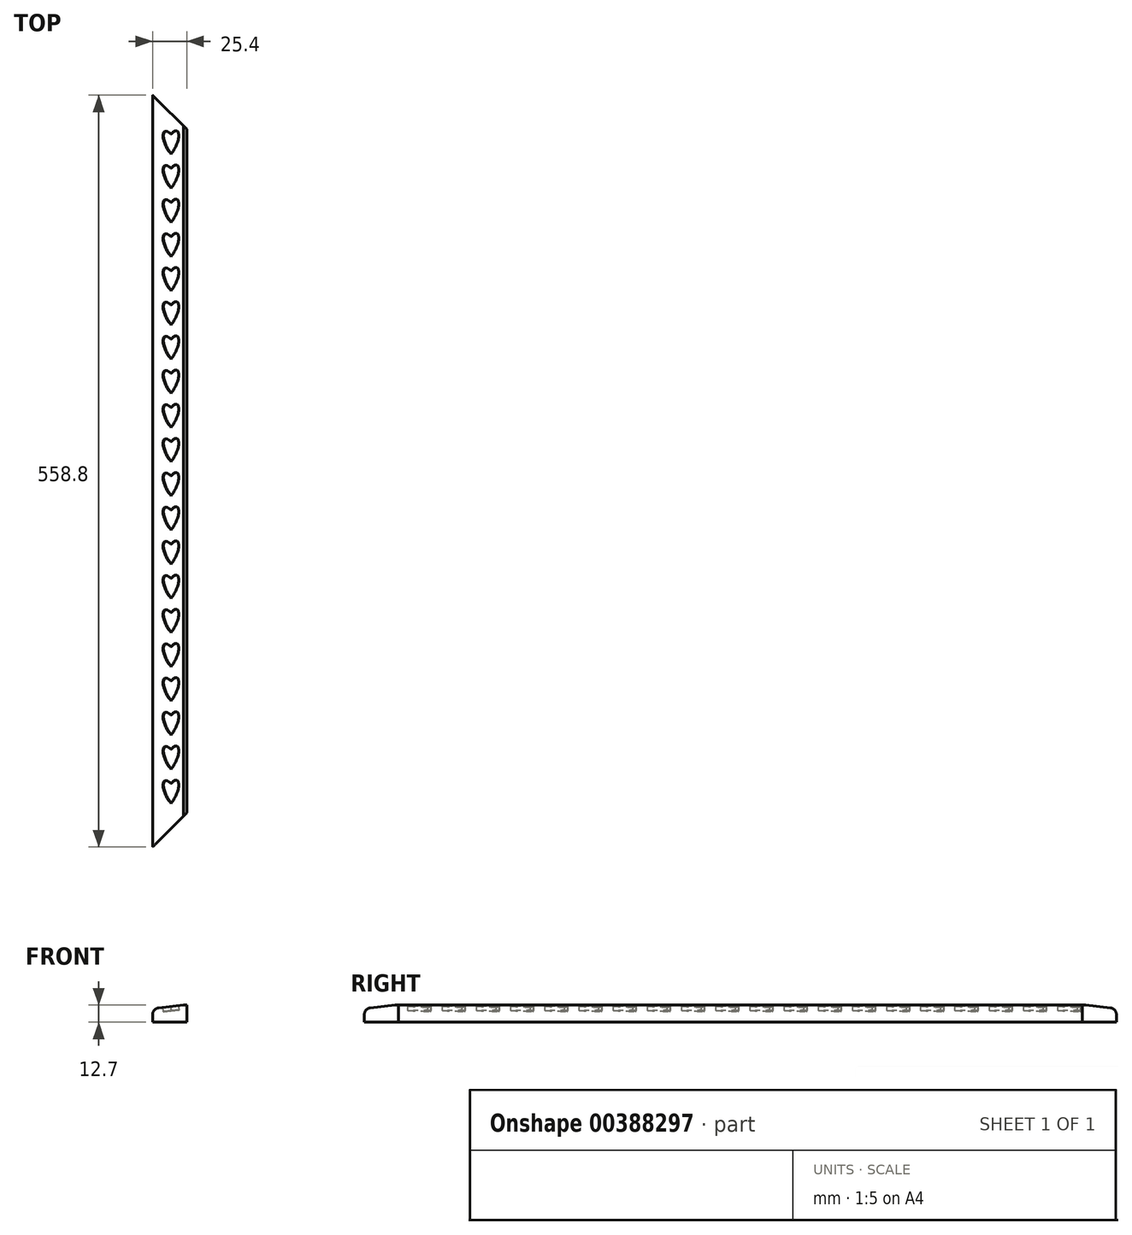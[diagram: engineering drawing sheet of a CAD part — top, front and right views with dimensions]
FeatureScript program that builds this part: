
annotation { "Feature Type Name" : "Feature", "Feature Type Description" : "" }
export const myFeature = defineFeature(function(context is Context, id is Id, definition is map)
    precondition{}
    {
        {
            var Q0;
            Q0=qCreatedBy(makeId("Top.planeOp"),FACE);
            var sketch = newSketch(context, id + "F0", { "sketchPlane" : qUnion([Q0])});
            skLineSegment(sketch, "E0.bottom", {"start": v(-12.7, 279.4) * mm, "end": v(12.7, 279.4) * mm});
            skLineSegment(sketch, "E0.top", {"start": v(-12.7, -279.4) * mm, "end": v(12.7, -279.4) * mm});
            skLineSegment(sketch, "E0.left", {"start": v(-12.7, 279.4) * mm, "end": v(-12.7, -279.4) * mm});
            skLineSegment(sketch, "E0.right", {"start": v(12.7, 279.4) * mm, "end": v(12.7, -279.4) * mm});
            skPoint(sketch, "E0.middle", {"position": v(0, 0) * mm});
            skLineSegment(sketch, "E1", {"start": v(-12.7, -279.4) * mm, "end": v(12.7, -254) * mm});
            skLineSegment(sketch, "E2.MirrorCS", {"start": v(-12.7, 279.4) * mm, "end": v(12.7, 254) * mm});
            skSolve(sketch);
        }
        {
            var Q0;
            Q0=makeQuery(id+"F0.imprint","IMPRINT",FACE,{"disambiguationData":[TD([[makeQuery(id+"F0.imprint","IMPRINT",EDGE,{"derivedFrom":sQuery(id+"F0.wireOp",EDGE,"E0.left")}),1.0]])]});
            extrude(context, id + "F1", {"entities" : qUnion([Q0]), "depth" : 12.7 * mm});
        }
        {
            var Q0;
            Q0=makeQuery(id+"F1.opExtrude","CAP_EDGE",EDGE,{"disambiguationData":[OSD([sQuery(id+"F0.wireOp",EDGE,"E0.left")])],"isStart":false});
            chamfer(context, id + "F2", {"entities" : qUnion([Q0]), "chamferType" : ChamferType.TWO_OFFSETS, "width1" : 2.54 * mm, "oppositeDirection" : true, "width2" : 22.86 * mm, "tangentPropagation" : true});
        }
        {
            var Q0;
            {var subQ0=sQuery(id+"F0.wireOp",EDGE,"E0.left");Q0=makeQuery(id+"F2.opChamfer","BLEND_EDGE",EDGE,{"blendedFrom":[makeQuery(id+"F1.opExtrude","CAP_EDGE",EDGE,{"disambiguationData":[OSD([subQ0])],"isStart":false}),makeQuery(id+"F1.opExtrude","SWEPT_FACE",FACE,{"disambiguationData":[OSD([subQ0])]})],"blendedInto":[makeQuery(id+"F1.opExtrude","SWEPT_FACE",FACE,{"disambiguationData":[OSD([subQ0])]})]});}
            fillet(context, id + "F3", {"entities" : qUnion([Q0]), "radius" : 5.08 * mm, "tangentPropagation" : true, "allowEdgeOverflow" : false});
        }
        {
            var Q0;
            Q0=makeQuery(id+"F2.opChamfer","BLEND_FACE",FACE,{"disambiguationData":[OSD([sQuery(id+"F0.wireOp",EDGE,"E0.left")])]});
            var sketch = newSketch(context, id + "F4", { "sketchPlane" : qUnion([Q0])});
            skLineSegment(sketch, "E3.bottom", {"start": v(-4.41, 253.3) * mm, "end": v(8.96, 253.3) * mm});
            skLineSegment(sketch, "E3.top", {"start": v(-4.41, 232.97) * mm, "end": v(8.96, 232.97) * mm});
            skLineSegment(sketch, "E3.left", {"start": v(-4.41, 253.3) * mm, "end": v(-4.41, 232.97) * mm});
            skLineSegment(sketch, "E3.right", {"start": v(8.96, 253.3) * mm, "end": v(8.96, 232.97) * mm});
            skEllipticalArc(sketch, "E4", {});
            skPoint(sketch, "E4.centerSnap0", {"position": v(-4.41, 243.13) * mm});
            skPoint(sketch, "E4.centerSnap1", {"position": v(2.27, 232.97) * mm});
            skEllipticalArc(sketch, "E5", {});
            skLineSegment(sketch, "E6", {"start": v(2.2, 250.5) * mm, "end": v(2.47, 250.22) * mm});
            skPoint(sketch, "E7.left.start.orphan", {"position": v(-6.95, 255.83) * mm});
            skLineSegment(sketch, "E8.0.1.0", {"start": v(-4.41, 227.9) * mm, "end": v(8.96, 227.9) * mm});
            skPoint(sketch, "E8.0.1.1", {"position": v(2.27, 207.57) * mm});
            skLineSegment(sketch, "E8.0.1.2", {"start": v(-4.41, 227.9) * mm, "end": v(-4.41, 207.57) * mm});
            skLineSegment(sketch, "E8.0.1.4", {"start": v(8.96, 227.9) * mm, "end": v(8.96, 207.57) * mm});
            skPoint(sketch, "E8.0.1.5", {"position": v(-4.41, 217.73) * mm});
            skEllipticalArc(sketch, "E8.0.1.6", {});
            skEllipticalArc(sketch, "E8.0.1.7", {});
            skLineSegment(sketch, "E8.0.1.8", {"start": v(-4.41, 207.57) * mm, "end": v(8.96, 207.57) * mm});
            skLineSegment(sketch, "E8.0.1.9", {"start": v(2.2, 225.1) * mm, "end": v(2.47, 224.82) * mm});
            skLineSegment(sketch, "E8.0.2.0", {"start": v(-4.41, 202.5) * mm, "end": v(8.96, 202.5) * mm});
            skPoint(sketch, "E8.0.2.1", {"position": v(2.27, 182.17) * mm});
            skLineSegment(sketch, "E8.0.2.2", {"start": v(-4.41, 202.5) * mm, "end": v(-4.41, 182.17) * mm});
            skPoint(sketch, "E8.0.2.3", {"position": v(-6.95, 230.43) * mm});
            skLineSegment(sketch, "E8.0.2.4", {"start": v(8.96, 202.5) * mm, "end": v(8.96, 182.17) * mm});
            skPoint(sketch, "E8.0.2.5", {"position": v(-4.41, 192.33) * mm});
            skEllipticalArc(sketch, "E8.0.2.6", {});
            skEllipticalArc(sketch, "E8.0.2.7", {});
            skLineSegment(sketch, "E8.0.2.8", {"start": v(-4.41, 182.17) * mm, "end": v(8.96, 182.17) * mm});
            skLineSegment(sketch, "E8.0.2.9", {"start": v(2.2, 199.7) * mm, "end": v(2.47, 199.42) * mm});
            skLineSegment(sketch, "E8.0.3.0", {"start": v(-4.41, 177.1) * mm, "end": v(8.96, 177.1) * mm});
            skPoint(sketch, "E8.0.3.1", {"position": v(2.27, 156.77) * mm});
            skLineSegment(sketch, "E8.0.3.2", {"start": v(-4.41, 177.1) * mm, "end": v(-4.41, 156.77) * mm});
            skPoint(sketch, "E8.0.3.3", {"position": v(-6.95, 205.03) * mm});
            skLineSegment(sketch, "E8.0.3.4", {"start": v(8.96, 177.1) * mm, "end": v(8.96, 156.77) * mm});
            skPoint(sketch, "E8.0.3.5", {"position": v(-4.41, 166.93) * mm});
            skEllipticalArc(sketch, "E8.0.3.6", {});
            skEllipticalArc(sketch, "E8.0.3.7", {});
            skLineSegment(sketch, "E8.0.3.8", {"start": v(-4.41, 156.77) * mm, "end": v(8.96, 156.77) * mm});
            skLineSegment(sketch, "E8.0.3.9", {"start": v(2.2, 174.3) * mm, "end": v(2.47, 174.02) * mm});
            skLineSegment(sketch, "E8.0.4.0", {"start": v(-4.41, 151.7) * mm, "end": v(8.96, 151.7) * mm});
            skPoint(sketch, "E8.0.4.1", {"position": v(2.27, 131.37) * mm});
            skLineSegment(sketch, "E8.0.4.2", {"start": v(-4.41, 151.7) * mm, "end": v(-4.41, 131.37) * mm});
            skPoint(sketch, "E8.0.4.3", {"position": v(-6.95, 179.63) * mm});
            skLineSegment(sketch, "E8.0.4.4", {"start": v(8.96, 151.7) * mm, "end": v(8.96, 131.37) * mm});
            skPoint(sketch, "E8.0.4.5", {"position": v(-4.41, 141.53) * mm});
            skEllipticalArc(sketch, "E8.0.4.6", {});
            skEllipticalArc(sketch, "E8.0.4.7", {});
            skLineSegment(sketch, "E8.0.4.8", {"start": v(-4.41, 131.37) * mm, "end": v(8.96, 131.37) * mm});
            skLineSegment(sketch, "E8.0.4.9", {"start": v(2.2, 148.9) * mm, "end": v(2.47, 148.62) * mm});
            skLineSegment(sketch, "E8.0.5.0", {"start": v(-4.41, 126.3) * mm, "end": v(8.96, 126.3) * mm});
            skPoint(sketch, "E8.0.5.1", {"position": v(2.27, 105.97) * mm});
            skLineSegment(sketch, "E8.0.5.2", {"start": v(-4.41, 126.3) * mm, "end": v(-4.41, 105.97) * mm});
            skPoint(sketch, "E8.0.5.3", {"position": v(-6.95, 154.23) * mm});
            skLineSegment(sketch, "E8.0.5.4", {"start": v(8.96, 126.3) * mm, "end": v(8.96, 105.97) * mm});
            skPoint(sketch, "E8.0.5.5", {"position": v(-4.41, 116.13) * mm});
            skEllipticalArc(sketch, "E8.0.5.6", {});
            skEllipticalArc(sketch, "E8.0.5.7", {});
            skLineSegment(sketch, "E8.0.5.8", {"start": v(-4.41, 105.97) * mm, "end": v(8.96, 105.97) * mm});
            skLineSegment(sketch, "E8.0.5.9", {"start": v(2.2, 123.5) * mm, "end": v(2.47, 123.22) * mm});
            skLineSegment(sketch, "E8.0.6.0", {"start": v(-4.41, 100.9) * mm, "end": v(8.96, 100.9) * mm});
            skPoint(sketch, "E8.0.6.1", {"position": v(2.27, 80.57) * mm});
            skLineSegment(sketch, "E8.0.6.2", {"start": v(-4.41, 100.9) * mm, "end": v(-4.41, 80.57) * mm});
            skPoint(sketch, "E8.0.6.3", {"position": v(-6.95, 128.83) * mm});
            skLineSegment(sketch, "E8.0.6.4", {"start": v(8.96, 100.9) * mm, "end": v(8.96, 80.57) * mm});
            skPoint(sketch, "E8.0.6.5", {"position": v(-4.41, 90.73) * mm});
            skEllipticalArc(sketch, "E8.0.6.6", {});
            skEllipticalArc(sketch, "E8.0.6.7", {});
            skLineSegment(sketch, "E8.0.6.8", {"start": v(-4.41, 80.57) * mm, "end": v(8.96, 80.57) * mm});
            skLineSegment(sketch, "E8.0.6.9", {"start": v(2.2, 98.1) * mm, "end": v(2.47, 97.82) * mm});
            skLineSegment(sketch, "E8.0.7.0", {"start": v(-4.41, 75.5) * mm, "end": v(8.96, 75.5) * mm});
            skPoint(sketch, "E8.0.7.1", {"position": v(2.27, 55.17) * mm});
            skLineSegment(sketch, "E8.0.7.2", {"start": v(-4.41, 75.5) * mm, "end": v(-4.41, 55.17) * mm});
            skPoint(sketch, "E8.0.7.3", {"position": v(-6.95, 103.43) * mm});
            skLineSegment(sketch, "E8.0.7.4", {"start": v(8.96, 75.5) * mm, "end": v(8.96, 55.17) * mm});
            skPoint(sketch, "E8.0.7.5", {"position": v(-4.41, 65.33) * mm});
            skEllipticalArc(sketch, "E8.0.7.6", {});
            skEllipticalArc(sketch, "E8.0.7.7", {});
            skLineSegment(sketch, "E8.0.7.8", {"start": v(-4.41, 55.17) * mm, "end": v(8.96, 55.17) * mm});
            skLineSegment(sketch, "E8.0.7.9", {"start": v(2.2, 72.7) * mm, "end": v(2.47, 72.42) * mm});
            skLineSegment(sketch, "E8.0.8.0", {"start": v(-4.41, 50.1) * mm, "end": v(8.96, 50.1) * mm});
            skPoint(sketch, "E8.0.8.1", {"position": v(2.27, 29.77) * mm});
            skLineSegment(sketch, "E8.0.8.2", {"start": v(-4.41, 50.1) * mm, "end": v(-4.41, 29.77) * mm});
            skPoint(sketch, "E8.0.8.3", {"position": v(-6.95, 78.03) * mm});
            skLineSegment(sketch, "E8.0.8.4", {"start": v(8.96, 50.1) * mm, "end": v(8.96, 29.77) * mm});
            skPoint(sketch, "E8.0.8.5", {"position": v(-4.41, 39.93) * mm});
            skEllipticalArc(sketch, "E8.0.8.6", {});
            skEllipticalArc(sketch, "E8.0.8.7", {});
            skLineSegment(sketch, "E8.0.8.8", {"start": v(-4.41, 29.77) * mm, "end": v(8.96, 29.77) * mm});
            skLineSegment(sketch, "E8.0.8.9", {"start": v(2.2, 47.3) * mm, "end": v(2.47, 47.02) * mm});
            skLineSegment(sketch, "E8.0.9.0", {"start": v(-4.41, 24.7) * mm, "end": v(8.96, 24.7) * mm});
            skPoint(sketch, "E8.0.9.1", {"position": v(2.27, 4.37) * mm});
            skLineSegment(sketch, "E8.0.9.2", {"start": v(-4.41, 24.7) * mm, "end": v(-4.41, 4.37) * mm});
            skPoint(sketch, "E8.0.9.3", {"position": v(-6.95, 52.63) * mm});
            skLineSegment(sketch, "E8.0.9.4", {"start": v(8.96, 24.7) * mm, "end": v(8.96, 4.37) * mm});
            skPoint(sketch, "E8.0.9.5", {"position": v(-4.41, 14.53) * mm});
            skEllipticalArc(sketch, "E8.0.9.6", {});
            skEllipticalArc(sketch, "E8.0.9.7", {});
            skLineSegment(sketch, "E8.0.9.8", {"start": v(-4.41, 4.37) * mm, "end": v(8.96, 4.37) * mm});
            skLineSegment(sketch, "E8.0.9.9", {"start": v(2.2, 21.9) * mm, "end": v(2.47, 21.62) * mm});
            skLineSegment(sketch, "E8.0.10.0", {"start": v(-4.41, -0.7) * mm, "end": v(8.96, -0.7) * mm});
            skPoint(sketch, "E8.0.10.1", {"position": v(2.27, -21.03) * mm});
            skLineSegment(sketch, "E8.0.10.2", {"start": v(-4.41, -0.7) * mm, "end": v(-4.41, -21.03) * mm});
            skPoint(sketch, "E8.0.10.3", {"position": v(-6.95, 27.23) * mm});
            skLineSegment(sketch, "E8.0.10.4", {"start": v(8.96, -0.7) * mm, "end": v(8.96, -21.03) * mm});
            skPoint(sketch, "E8.0.10.5", {"position": v(-4.41, -10.87) * mm});
            skEllipticalArc(sketch, "E8.0.10.6", {});
            skEllipticalArc(sketch, "E8.0.10.7", {});
            skLineSegment(sketch, "E8.0.10.8", {"start": v(-4.41, -21.03) * mm, "end": v(8.96, -21.03) * mm});
            skLineSegment(sketch, "E8.0.10.9", {"start": v(2.2, -3.5) * mm, "end": v(2.47, -3.78) * mm});
            skLineSegment(sketch, "E8.0.11.0", {"start": v(-4.41, -26.1) * mm, "end": v(8.96, -26.1) * mm});
            skPoint(sketch, "E8.0.11.1", {"position": v(2.27, -46.43) * mm});
            skLineSegment(sketch, "E8.0.11.2", {"start": v(-4.41, -26.1) * mm, "end": v(-4.41, -46.43) * mm});
            skPoint(sketch, "E8.0.11.3", {"position": v(-6.95, 1.83) * mm});
            skLineSegment(sketch, "E8.0.11.4", {"start": v(8.96, -26.1) * mm, "end": v(8.96, -46.43) * mm});
            skPoint(sketch, "E8.0.11.5", {"position": v(-4.41, -36.27) * mm});
            skEllipticalArc(sketch, "E8.0.11.6", {});
            skEllipticalArc(sketch, "E8.0.11.7", {});
            skLineSegment(sketch, "E8.0.11.8", {"start": v(-4.41, -46.43) * mm, "end": v(8.96, -46.43) * mm});
            skLineSegment(sketch, "E8.0.11.9", {"start": v(2.2, -28.9) * mm, "end": v(2.47, -29.18) * mm});
            skLineSegment(sketch, "E8.0.12.0", {"start": v(-4.41, -51.5) * mm, "end": v(8.96, -51.5) * mm});
            skPoint(sketch, "E8.0.12.1", {"position": v(2.27, -71.83) * mm});
            skLineSegment(sketch, "E8.0.12.2", {"start": v(-4.41, -51.5) * mm, "end": v(-4.41, -71.83) * mm});
            skPoint(sketch, "E8.0.12.3", {"position": v(-6.95, -23.57) * mm});
            skLineSegment(sketch, "E8.0.12.4", {"start": v(8.96, -51.5) * mm, "end": v(8.96, -71.83) * mm});
            skPoint(sketch, "E8.0.12.5", {"position": v(-4.41, -61.67) * mm});
            skEllipticalArc(sketch, "E8.0.12.6", {});
            skEllipticalArc(sketch, "E8.0.12.7", {});
            skLineSegment(sketch, "E8.0.12.8", {"start": v(-4.41, -71.83) * mm, "end": v(8.96, -71.83) * mm});
            skLineSegment(sketch, "E8.0.12.9", {"start": v(2.2, -54.3) * mm, "end": v(2.47, -54.58) * mm});
            skLineSegment(sketch, "E8.0.13.0", {"start": v(-4.41, -76.9) * mm, "end": v(8.96, -76.9) * mm});
            skPoint(sketch, "E8.0.13.1", {"position": v(2.27, -97.23) * mm});
            skLineSegment(sketch, "E8.0.13.2", {"start": v(-4.41, -76.9) * mm, "end": v(-4.41, -97.23) * mm});
            skPoint(sketch, "E8.0.13.3", {"position": v(-6.95, -48.97) * mm});
            skLineSegment(sketch, "E8.0.13.4", {"start": v(8.96, -76.9) * mm, "end": v(8.96, -97.23) * mm});
            skPoint(sketch, "E8.0.13.5", {"position": v(-4.41, -87.07) * mm});
            skEllipticalArc(sketch, "E8.0.13.6", {});
            skEllipticalArc(sketch, "E8.0.13.7", {});
            skLineSegment(sketch, "E8.0.13.8", {"start": v(-4.41, -97.23) * mm, "end": v(8.96, -97.23) * mm});
            skLineSegment(sketch, "E8.0.13.9", {"start": v(2.2, -79.7) * mm, "end": v(2.47, -79.98) * mm});
            skLineSegment(sketch, "E8.0.14.0", {"start": v(-4.41, -102.3) * mm, "end": v(8.96, -102.3) * mm});
            skPoint(sketch, "E8.0.14.1", {"position": v(2.27, -122.63) * mm});
            skLineSegment(sketch, "E8.0.14.2", {"start": v(-4.41, -102.3) * mm, "end": v(-4.41, -122.63) * mm});
            skPoint(sketch, "E8.0.14.3", {"position": v(-6.95, -74.37) * mm});
            skLineSegment(sketch, "E8.0.14.4", {"start": v(8.96, -102.3) * mm, "end": v(8.96, -122.63) * mm});
            skPoint(sketch, "E8.0.14.5", {"position": v(-4.41, -112.47) * mm});
            skEllipticalArc(sketch, "E8.0.14.6", {});
            skEllipticalArc(sketch, "E8.0.14.7", {});
            skLineSegment(sketch, "E8.0.14.8", {"start": v(-4.41, -122.63) * mm, "end": v(8.96, -122.63) * mm});
            skLineSegment(sketch, "E8.0.14.9", {"start": v(2.2, -105.1) * mm, "end": v(2.47, -105.38) * mm});
            skLineSegment(sketch, "E8.0.15.0", {"start": v(-4.41, -127.7) * mm, "end": v(8.96, -127.7) * mm});
            skPoint(sketch, "E8.0.15.1", {"position": v(2.27, -148.03) * mm});
            skLineSegment(sketch, "E8.0.15.2", {"start": v(-4.41, -127.7) * mm, "end": v(-4.41, -148.03) * mm});
            skPoint(sketch, "E8.0.15.3", {"position": v(-6.95, -99.77) * mm});
            skLineSegment(sketch, "E8.0.15.4", {"start": v(8.96, -127.7) * mm, "end": v(8.96, -148.03) * mm});
            skPoint(sketch, "E8.0.15.5", {"position": v(-4.41, -137.87) * mm});
            skEllipticalArc(sketch, "E8.0.15.6", {});
            skEllipticalArc(sketch, "E8.0.15.7", {});
            skLineSegment(sketch, "E8.0.15.8", {"start": v(-4.41, -148.03) * mm, "end": v(8.96, -148.03) * mm});
            skLineSegment(sketch, "E8.0.15.9", {"start": v(2.2, -130.5) * mm, "end": v(2.47, -130.78) * mm});
            skLineSegment(sketch, "E8.0.16.0", {"start": v(-4.41, -153.1) * mm, "end": v(8.96, -153.1) * mm});
            skPoint(sketch, "E8.0.16.1", {"position": v(2.27, -173.43) * mm});
            skLineSegment(sketch, "E8.0.16.2", {"start": v(-4.41, -153.1) * mm, "end": v(-4.41, -173.43) * mm});
            skPoint(sketch, "E8.0.16.3", {"position": v(-6.95, -125.17) * mm});
            skLineSegment(sketch, "E8.0.16.4", {"start": v(8.96, -153.1) * mm, "end": v(8.96, -173.43) * mm});
            skPoint(sketch, "E8.0.16.5", {"position": v(-4.41, -163.27) * mm});
            skEllipticalArc(sketch, "E8.0.16.6", {});
            skEllipticalArc(sketch, "E8.0.16.7", {});
            skLineSegment(sketch, "E8.0.16.8", {"start": v(-4.41, -173.43) * mm, "end": v(8.96, -173.43) * mm});
            skLineSegment(sketch, "E8.0.16.9", {"start": v(2.2, -155.9) * mm, "end": v(2.47, -156.18) * mm});
            skLineSegment(sketch, "E8.0.17.0", {"start": v(-4.41, -178.5) * mm, "end": v(8.96, -178.5) * mm});
            skPoint(sketch, "E8.0.17.1", {"position": v(2.27, -198.83) * mm});
            skLineSegment(sketch, "E8.0.17.2", {"start": v(-4.41, -178.5) * mm, "end": v(-4.41, -198.83) * mm});
            skPoint(sketch, "E8.0.17.3", {"position": v(-6.95, -150.57) * mm});
            skLineSegment(sketch, "E8.0.17.4", {"start": v(8.96, -178.5) * mm, "end": v(8.96, -198.83) * mm});
            skPoint(sketch, "E8.0.17.5", {"position": v(-4.41, -188.67) * mm});
            skEllipticalArc(sketch, "E8.0.17.6", {});
            skEllipticalArc(sketch, "E8.0.17.7", {});
            skLineSegment(sketch, "E8.0.17.8", {"start": v(-4.41, -198.83) * mm, "end": v(8.96, -198.83) * mm});
            skLineSegment(sketch, "E8.0.17.9", {"start": v(2.2, -181.3) * mm, "end": v(2.47, -181.58) * mm});
            skLineSegment(sketch, "E8.direction1", {"start": v(-4.41, 232.97) * mm, "end": v(20.99, 232.97) * mm, "construction": true});
            skLineSegment(sketch, "E8.direction2", {"start": v(-4.41, 232.97) * mm, "end": v(-4.41, 207.57) * mm, "construction": true});
            skPoint(sketch, "E9.0.1.0", {"position": v(2.27, -224.23) * mm});
            skPoint(sketch, "E9.0.1.2", {"position": v(-4.41, -214.07) * mm});
            skLineSegment(sketch, "E9.0.1.3", {"start": v(-4.41, -203.9) * mm, "end": v(8.96, -203.9) * mm});
            skLineSegment(sketch, "E9.0.1.4", {"start": v(-4.41, -203.9) * mm, "end": v(-4.41, -224.23) * mm});
            skLineSegment(sketch, "E9.0.1.5", {"start": v(8.96, -203.9) * mm, "end": v(8.96, -224.23) * mm});
            skEllipticalArc(sketch, "E9.0.1.6", {});
            skEllipticalArc(sketch, "E9.0.1.7", {});
            skLineSegment(sketch, "E9.0.1.8", {"start": v(-4.41, -224.23) * mm, "end": v(8.96, -224.23) * mm});
            skLineSegment(sketch, "E9.0.1.9", {"start": v(2.2, -206.7) * mm, "end": v(2.47, -206.98) * mm});
            skPoint(sketch, "E9.0.2.0", {"position": v(2.27, -249.63) * mm});
            skPoint(sketch, "E9.0.2.1", {"position": v(2.27, -224.23) * mm});
            skPoint(sketch, "E9.0.2.2", {"position": v(-4.41, -239.47) * mm});
            skLineSegment(sketch, "E9.0.2.3", {"start": v(-4.41, -229.3) * mm, "end": v(8.96, -229.3) * mm});
            skLineSegment(sketch, "E9.0.2.4", {"start": v(-4.41, -229.3) * mm, "end": v(-4.41, -249.63) * mm});
            skLineSegment(sketch, "E9.0.2.5", {"start": v(8.96, -229.3) * mm, "end": v(8.96, -249.63) * mm});
            skEllipticalArc(sketch, "E9.0.2.6", {});
            skEllipticalArc(sketch, "E9.0.2.7", {});
            skLineSegment(sketch, "E9.0.2.8", {"start": v(-4.41, -249.63) * mm, "end": v(8.96, -249.63) * mm});
            skLineSegment(sketch, "E9.0.2.9", {"start": v(2.2, -232.1) * mm, "end": v(2.47, -232.38) * mm});
            skLineSegment(sketch, "E9.direction1", {"start": v(-4.41, -198.83) * mm, "end": v(20.99, -198.83) * mm, "construction": true});
            skLineSegment(sketch, "E9.direction2", {"start": v(-4.41, -198.83) * mm, "end": v(-4.41, -224.23) * mm, "construction": true});
            const initialGuessF4  = {"E4": [0.002273408694541042, 0.24313099215246017, -0.44549528212436185, 0.8952842864727022, 0.0104013, 0.0041656, 5.4030752140367095, 2.2614825604469164], "E5": [0.002273408694541042, 0.24313099215246017, 0.42639124113221455, 0.9045388380195346, 0.0106934, 0.004089400000000001, 4.043989840250925, 0.902397186661131], "E8.0.1.6": [0.002273408694541042, 0.21773099215246017, 0.42639124113221455, 0.9045388380195346, 0.0106934, 0.004089400000000001, 4.043989840250925, 0.9023971866611309], "E8.0.1.7": [0.002273408694541042, 0.21773099215246017, -0.44549528212436185, 0.8952842864727022, 0.0104013, 0.0041656, 5.4030752140367095, 2.2614825604469164], "E8.0.2.6": [0.002273408694541042, 0.19233099215246016, 0.42639124113221455, 0.9045388380195346, 0.0106934, 0.004089400000000001, 4.043989840250925, 0.9023971866611309], "E8.0.2.7": [0.002273408694541042, 0.19233099215246016, -0.44549528212436185, 0.8952842864727022, 0.0104013, 0.0041656, 5.4030752140367095, 2.2614825604469164], "E8.0.3.6": [0.002273408694541042, 0.16693099215246016, 0.42639124113221455, 0.9045388380195346, 0.0106934, 0.004089400000000001, 4.043989840250925, 0.9023971866611309], "E8.0.3.7": [0.002273408694541042, 0.16693099215246016, -0.44549528212436185, 0.8952842864727022, 0.0104013, 0.0041656, 5.4030752140367095, 2.2614825604469164], "E8.0.4.6": [0.002273408694541042, 0.14153099215246015, 0.42639124113221455, 0.9045388380195346, 0.0106934, 0.004089400000000001, 4.043989840250925, 0.9023971866611309], "E8.0.4.7": [0.002273408694541042, 0.14153099215246015, -0.44549528212436185, 0.8952842864727022, 0.0104013, 0.0041656, 5.4030752140367095, 2.2614825604469164], "E8.0.5.6": [0.002273408694541042, 0.11613099215246014, 0.42639124113221455, 0.9045388380195346, 0.0106934, 0.004089400000000001, 4.043989840250925, 0.9023971866611309], "E8.0.5.7": [0.002273408694541042, 0.11613099215246014, -0.44549528212436185, 0.8952842864727022, 0.0104013, 0.0041656, 5.4030752140367095, 2.2614825604469164], "E8.0.6.6": [0.002273408694541042, 0.09073099215246014, 0.42639124113221455, 0.9045388380195346, 0.0106934, 0.004089400000000001, 4.043989840250925, 0.9023971866611309], "E8.0.6.7": [0.002273408694541042, 0.09073099215246014, -0.44549528212436185, 0.8952842864727022, 0.0104013, 0.0041656, 5.4030752140367095, 2.2614825604469164], "E8.0.7.6": [0.002273408694541042, 0.06533099215246013, 0.42639124113221455, 0.9045388380195346, 0.0106934, 0.004089400000000001, 4.043989840250925, 0.9023971866611309], "E8.0.7.7": [0.002273408694541042, 0.06533099215246013, -0.44549528212436185, 0.8952842864727022, 0.0104013, 0.0041656, 5.4030752140367095, 2.2614825604469164], "E8.0.8.6": [0.002273408694541042, 0.039930992152460126, 0.42639124113221455, 0.9045388380195346, 0.0106934, 0.004089400000000001, 4.043989840250925, 0.9023971866611309], "E8.0.8.7": [0.002273408694541042, 0.039930992152460126, -0.44549528212436185, 0.8952842864727022, 0.0104013, 0.0041656, 5.4030752140367095, 2.261482560446917], "E8.0.9.6": [0.002273408694541042, 0.014530992152460117, 0.42639124113221455, 0.9045388380195346, 0.0106934, 0.004089400000000001, 4.043989840250925, 0.9023971866611309], "E8.0.9.7": [0.002273408694541042, 0.014530992152460117, -0.44549528212436185, 0.8952842864727022, 0.0104013, 0.0041656, 5.4030752140367095, 2.2614825604469164], "E8.0.10.6": [0.002273408694541042, -0.010869007847539889, 0.42639124113221455, 0.9045388380195346, 0.0106934, 0.004089400000000001, 4.043989840250925, 0.9023971866611309], "E8.0.10.7": [0.002273408694541042, -0.010869007847539889, -0.44549528212436185, 0.8952842864727022, 0.0104013, 0.0041656, 5.4030752140367095, 2.2614825604469164], "E8.0.11.6": [0.002273408694541042, -0.03626900784753992, 0.42639124113221455, 0.9045388380195346, 0.0106934, 0.004089400000000001, 4.043989840250925, 0.9023971866611309], "E8.0.11.7": [0.002273408694541042, -0.03626900784753992, -0.44549528212436185, 0.8952842864727022, 0.0104013, 0.0041656, 5.4030752140367095, 2.2614825604469164], "E8.0.12.6": [0.002273408694541042, -0.0616690078475399, 0.42639124113221455, 0.9045388380195346, 0.0106934, 0.004089400000000001, 4.043989840250925, 0.9023971866611309], "E8.0.12.7": [0.002273408694541042, -0.0616690078475399, -0.44549528212436185, 0.8952842864727022, 0.0104013, 0.0041656, 5.4030752140367095, 2.2614825604469164], "E8.0.13.6": [0.002273408694541042, -0.08706900784753988, 0.42639124113221455, 0.9045388380195346, 0.0106934, 0.004089400000000001, 4.043989840250925, 0.9023971866611309], "E8.0.13.7": [0.002273408694541042, -0.08706900784753988, -0.44549528212436185, 0.8952842864727022, 0.0104013, 0.0041656, 5.4030752140367095, 2.2614825604469164], "E8.0.14.6": [0.002273408694541042, -0.11246900784753991, 0.42639124113221455, 0.9045388380195346, 0.0106934, 0.004089400000000001, 4.043989840250925, 0.9023971866611309], "E8.0.14.7": [0.002273408694541042, -0.11246900784753991, -0.44549528212436185, 0.8952842864727022, 0.0104013, 0.0041656, 5.4030752140367095, 2.2614825604469164], "E8.0.15.6": [0.002273408694541042, -0.13786900784753994, 0.42639124113221455, 0.9045388380195346, 0.0106934, 0.004089400000000001, 4.043989840250925, 0.9023971866611309], "E8.0.15.7": [0.002273408694541042, -0.13786900784753994, -0.44549528212436185, 0.8952842864727022, 0.0104013, 0.0041656, 5.4030752140367095, 2.2614825604469164], "E8.0.16.6": [0.002273408694541042, -0.16326900784753992, 0.42639124113221455, 0.9045388380195346, 0.0106934, 0.004089400000000001, 4.043989840250925, 0.9023971866611309], "E8.0.16.7": [0.002273408694541042, -0.16326900784753992, -0.44549528212436185, 0.8952842864727022, 0.0104013, 0.0041656, 5.4030752140367095, 2.2614825604469164], "E8.0.17.6": [0.002273408694541042, -0.1886690078475399, 0.42639124113221455, 0.9045388380195346, 0.0106934, 0.004089400000000001, 4.043989840250925, 0.9023971866611309], "E8.0.17.7": [0.002273408694541042, -0.1886690078475399, -0.44549528212436185, 0.8952842864727022, 0.0104013, 0.0041656, 5.4030752140367095, 2.2614825604469164], "E9.0.1.6": [0.002273408694541042, -0.2140690078475399, 0.42639124113221455, 0.9045388380195346, 0.0106934, 0.004089400000000001, 4.043989840250925, 0.9023971866611308], "E9.0.1.7": [0.002273408694541042, -0.2140690078475399, -0.44549528212436185, 0.8952842864727022, 0.0104013, 0.0041656, 5.4030752140367095, 2.2614825604469164], "E9.0.2.6": [0.002273408694541042, -0.2394690078475399, 0.42639124113221455, 0.9045388380195346, 0.0106934, 0.004089400000000001, 4.043989840250925, 0.9023971866611308], "E9.0.2.7": [0.002273408694541042, -0.2394690078475399, -0.44549528212436185, 0.8952842864727022, 0.0104013, 0.0041656, 5.4030752140367095, 2.2614825604469164]};
            skSetInitialGuess(sketch, initialGuessF4);
            skSolve(sketch);
        }
        {
            var Q0;
            Q0=makeQuery(id+"F4.imprint","IMPRINT",FACE,{"disambiguationData":[TD([[makeQuery(id+"F4.imprint","IMPRINT",EDGE,{"derivedFrom":sQuery(id+"F4.wireOp",EDGE,"E4")}),1.0]])]});
            var Q1;
            Q1=makeQuery(id+"F4.imprint","IMPRINT",FACE,{"disambiguationData":[TD([[makeQuery(id+"F4.imprint","IMPRINT",EDGE,{"derivedFrom":sQuery(id+"F4.wireOp",EDGE,"E8.0.1.6")}),1.0]])]});
            var Q2;
            Q2=makeQuery(id+"F4.imprint","IMPRINT",FACE,{"disambiguationData":[TD([[makeQuery(id+"F4.imprint","IMPRINT",EDGE,{"derivedFrom":sQuery(id+"F4.wireOp",EDGE,"E8.0.2.6")}),1.0]])]});
            var Q3;
            Q3=makeQuery(id+"F4.imprint","IMPRINT",FACE,{"disambiguationData":[TD([[makeQuery(id+"F4.imprint","IMPRINT",EDGE,{"derivedFrom":sQuery(id+"F4.wireOp",EDGE,"E8.0.3.6")}),1.0]])]});
            var Q4;
            Q4=makeQuery(id+"F4.imprint","IMPRINT",FACE,{"disambiguationData":[TD([[makeQuery(id+"F4.imprint","IMPRINT",EDGE,{"derivedFrom":sQuery(id+"F4.wireOp",EDGE,"E8.0.4.6")}),1.0]])]});
            var Q5;
            Q5=makeQuery(id+"F4.imprint","IMPRINT",FACE,{"disambiguationData":[TD([[makeQuery(id+"F4.imprint","IMPRINT",EDGE,{"derivedFrom":sQuery(id+"F4.wireOp",EDGE,"E8.0.5.6")}),1.0]])]});
            var Q6;
            Q6=makeQuery(id+"F4.imprint","IMPRINT",FACE,{"disambiguationData":[TD([[makeQuery(id+"F4.imprint","IMPRINT",EDGE,{"derivedFrom":sQuery(id+"F4.wireOp",EDGE,"E8.0.6.6")}),1.0]])]});
            var Q7;
            Q7=makeQuery(id+"F4.imprint","IMPRINT",FACE,{"disambiguationData":[TD([[makeQuery(id+"F4.imprint","IMPRINT",EDGE,{"derivedFrom":sQuery(id+"F4.wireOp",EDGE,"E8.0.7.6")}),1.0]])]});
            var Q8;
            Q8=makeQuery(id+"F4.imprint","IMPRINT",FACE,{"disambiguationData":[TD([[makeQuery(id+"F4.imprint","IMPRINT",EDGE,{"derivedFrom":sQuery(id+"F4.wireOp",EDGE,"E8.0.8.6")}),1.0]])]});
            var Q9;
            Q9=makeQuery(id+"F4.imprint","IMPRINT",FACE,{"disambiguationData":[TD([[makeQuery(id+"F4.imprint","IMPRINT",EDGE,{"derivedFrom":sQuery(id+"F4.wireOp",EDGE,"E8.0.9.6")}),1.0]])]});
            var Q10;
            Q10=makeQuery(id+"F4.imprint","IMPRINT",FACE,{"disambiguationData":[TD([[makeQuery(id+"F4.imprint","IMPRINT",EDGE,{"derivedFrom":sQuery(id+"F4.wireOp",EDGE,"E8.0.10.6")}),1.0]])]});
            var Q11;
            Q11=makeQuery(id+"F4.imprint","IMPRINT",FACE,{"disambiguationData":[TD([[makeQuery(id+"F4.imprint","IMPRINT",EDGE,{"derivedFrom":sQuery(id+"F4.wireOp",EDGE,"E8.0.11.6")}),1.0]])]});
            var Q12;
            Q12=makeQuery(id+"F4.imprint","IMPRINT",FACE,{"disambiguationData":[TD([[makeQuery(id+"F4.imprint","IMPRINT",EDGE,{"derivedFrom":sQuery(id+"F4.wireOp",EDGE,"E8.0.12.6")}),1.0]])]});
            var Q13;
            Q13=makeQuery(id+"F4.imprint","IMPRINT",FACE,{"disambiguationData":[TD([[makeQuery(id+"F4.imprint","IMPRINT",EDGE,{"derivedFrom":sQuery(id+"F4.wireOp",EDGE,"E8.0.13.6")}),1.0]])]});
            var Q14;
            Q14=makeQuery(id+"F4.imprint","IMPRINT",FACE,{"disambiguationData":[TD([[makeQuery(id+"F4.imprint","IMPRINT",EDGE,{"derivedFrom":sQuery(id+"F4.wireOp",EDGE,"E8.0.14.6")}),1.0]])]});
            var Q15;
            Q15=makeQuery(id+"F4.imprint","IMPRINT",FACE,{"disambiguationData":[TD([[makeQuery(id+"F4.imprint","IMPRINT",EDGE,{"derivedFrom":sQuery(id+"F4.wireOp",EDGE,"E8.0.15.6")}),1.0]])]});
            var Q16;
            Q16=makeQuery(id+"F4.imprint","IMPRINT",FACE,{"disambiguationData":[TD([[makeQuery(id+"F4.imprint","IMPRINT",EDGE,{"derivedFrom":sQuery(id+"F4.wireOp",EDGE,"E8.0.16.6")}),1.0]])]});
            var Q17;
            Q17=makeQuery(id+"F4.imprint","IMPRINT",FACE,{"disambiguationData":[TD([[makeQuery(id+"F4.imprint","IMPRINT",EDGE,{"derivedFrom":sQuery(id+"F4.wireOp",EDGE,"E8.0.17.6")}),1.0]])]});
            var Q18;
            Q18=makeQuery(id+"F4.imprint","IMPRINT",FACE,{"disambiguationData":[TD([[makeQuery(id+"F4.imprint","IMPRINT",EDGE,{"derivedFrom":sQuery(id+"F4.wireOp",EDGE,"E9.0.1.6")}),1.0]])]});
            var Q19;
            Q19=makeQuery(id+"F4.imprint","IMPRINT",FACE,{"disambiguationData":[TD([[makeQuery(id+"F4.imprint","IMPRINT",EDGE,{"derivedFrom":sQuery(id+"F4.wireOp",EDGE,"E9.0.2.6")}),1.0]])]});
            extrude(context, id + "F5", {"entities" : qUnion([Q0, Q1, Q2, Q3, Q4, Q5, Q6, Q7, Q8, Q9, Q10, Q11, Q12, Q13, Q14, Q15, Q16, Q17, Q18, Q19]), "operationType" : NewBodyOperationType.REMOVE, "oppositeDirection" : true, "depth" : 3.17 * mm});
        }
    });
